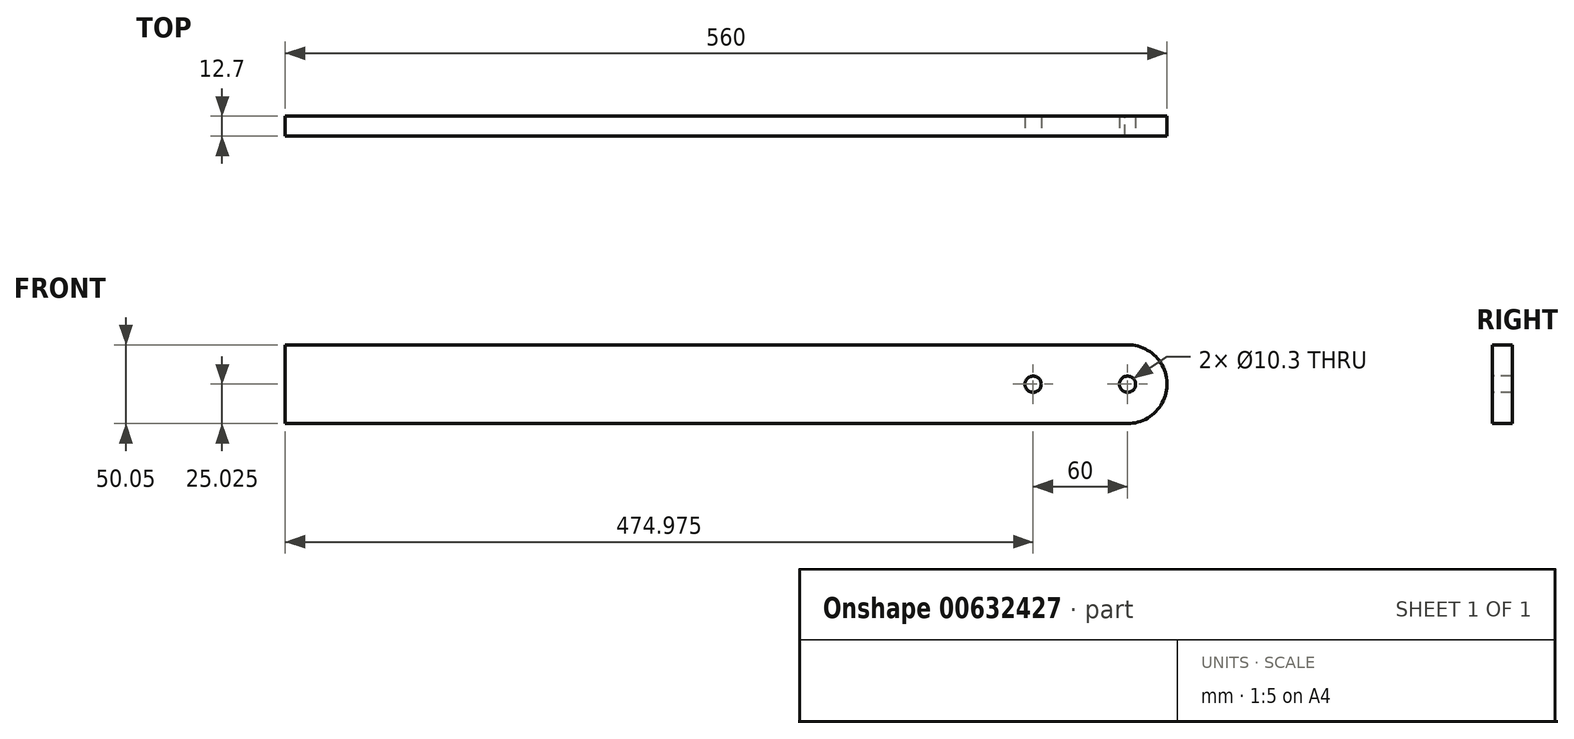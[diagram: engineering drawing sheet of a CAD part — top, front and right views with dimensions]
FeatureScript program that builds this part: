
annotation { "Feature Type Name" : "Feature", "Feature Type Description" : "" }
export const myFeature = defineFeature(function(context is Context, id is Id, definition is map)
    precondition{}
    {
        {
            var Q0;
            Q0=qCreatedBy(makeId("Front.planeOp"),FACE);
            var sketch = newSketch(context, id + "F0", { "sketchPlane" : qUnion([Q0])});
            skLineSegment(sketch, "E0.bottom", {"start": v(0, 0) * mm, "end": v(533.4, 0) * mm});
            skLineSegment(sketch, "E0.top", {"start": v(0, 50) * mm, "end": v(534.98, 50) * mm});
            skLineSegment(sketch, "E0.left", {"start": v(0, 0) * mm, "end": v(0, 50) * mm});
            skArc(sketch, "E1", {"start": v(533.4, 0) * mm, "mid": v(559.99, 24.19) * mm, "end": v(534.98, 50) * mm});
            skPoint(sketch, "E2", {"position": v(474.98, 24.98) * mm});
            skSolve(sketch);
        }
        {
            var Q0;
            Q0=makeQuery(id+"F0.imprint","IMPRINT",FACE,{"disambiguationData":[TD([[makeQuery(id+"F0.imprint","IMPRINT",EDGE,{"derivedFrom":sQuery(id+"F0.wireOp",EDGE,"E0.bottom")}),1.0]])]});
            extrude(context, id + "F1", {"entities" : qUnion([Q0]), "depth" : 12.7 * mm, "offsetDistance" : 25 * mm});
        }
        {
            var Q0;
            Q0=sQuery(id+"F0.wireOp",VERTEX,"E2");
            var Q1;
            Q1=sQuery(id+"F0.wireOp",VERTEX,"E1.center");
            var Q2;
            Q2=makeQuery(id+"F1.opExtrude","SWEPT_BODY",BODY,{"disambiguationData":[OSD([sQuery(id+"F0.wireOp",EDGE,"E0.bottom"),sQuery(id+"F0.wireOp",EDGE,"E0.top"),sQuery(id+"F0.wireOp",EDGE,"E0.left"),sQuery(id+"F0.wireOp",EDGE,"E1")])]});
            hole(context, id + "F2", {"style" : HoleStyle.SIMPLE, "endStyle" : HoleEndStyle.THROUGH, "oppositeDirection" : true, "standardTappedOrClearance" : lookupTablePath({ "standard" : "ISO", "engagement" : "75%", "pitch" : "1.75 mm", "size" : "M12", "type" : "Tapped" }), "standardBlindInLast" : lookupTablePath({ "standard" : "ISO", "engagement" : "75%", "pitch" : "1.75 mm", "size" : "M12", "type" : "Tapped" }), "holeDiameter" : 10.3 * mm, "majorDiameter" : 12 * mm, "showTappedDepth" : true, "isTappedThrough" : true, "tappedDepth" : 12 * mm, "tapClearance" : 3, "startFromSketch" : true, "locations" : qUnion([Q0, Q1]), "scope" : qUnion([Q2])});
        }
    });
